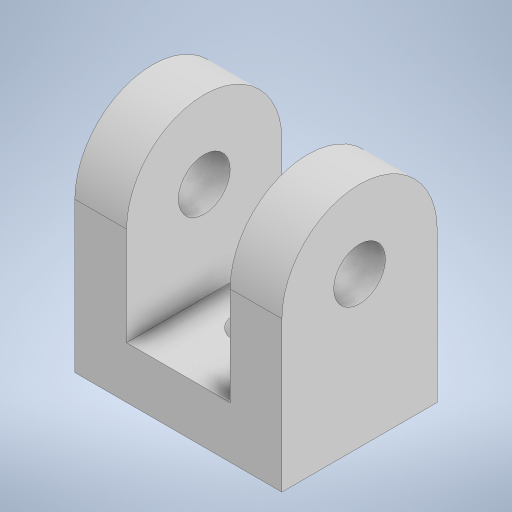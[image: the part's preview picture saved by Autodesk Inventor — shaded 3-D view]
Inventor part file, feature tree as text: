
AUTODESK INVENTOR PART (.ipt)
format: ipt  version: 2023.2 (Build 272271030, 271C)  size: 235,520 bytes
history: native  units: mm
features: extrude x3, sketch x3, projected_geometry x2
ambient origin geometry x8: Origin, YZ Plane, XZ Plane, XY Plane, X Axis, Y Axis, Z Axis, Center Point
bodies: Solid1 (feature_tree)
feature tree (8):
  extrude  "Extrusion1"  Depth=10.0mm
  extrude  "Extrusion2"  Depth=40.0mm TaperAngle=0.0deg
  extrude  "Extrusion3"  Depth=10.0mm
  sketch  "Sketch1"  dims[d0=15.0mm d1=10.0mm]
  sketch  "Sketch2"  dims[d2=29.0mm d3=40.0mm d4=0.0mm]
  projected_geometry  "Projected Loop1"
  projected_geometry  "Projected Loop2"
  sketch  "Sketch3"  dims[d5=20.0mm d6=10.0mm d7=34.0mm d8=40.0mm d9=0.0mm d10=8.6mm d11=0.0mm d12=0.0mm]
